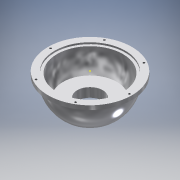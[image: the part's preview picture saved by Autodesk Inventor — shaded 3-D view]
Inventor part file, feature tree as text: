
AUTODESK INVENTOR PART (.ipt)
format: ipt  version: 2016 (Build 200138000, 138)  size: 551,424 bytes
history: native  units: mm
features: projected_geometry x22, sketch x21, extrude x16, plane x11, hole x5, mirror x3, loft x2, chamfer x2, pattern_circular x2, revolve x1, other x1
ambient origin geometry x8: Origin, YZ Plane, XZ Plane, XY Plane, X Axis, Y Axis, Z Axis, Center Point
bodies: Volumenkörper1 (feature_tree)
feature tree (86):
  revolve  "Umdrehung1"
  sketch  "Skizze6"  dims[d7=5.0mm d8=90.0deg]
  plane  "Arbeitsebene2"
  sketch  "Skizze7"  dims[d36=4.0mm d38=2.0mm]
  plane  "Arbeitsebene3"
  sketch  "Skizze8"  dims[d40=1.2mm d41=45.0mm]
  loft  "Erhebung1"
  extrude  "Extrusion16"  TaperAngle=90.0deg  [1 undecoded]
  other  "Rippe1"
  extrude  "Extrusion17"  Depth=2.0mm
  extrude  "Extrusion21"  Depth=45.0mm
  hole  "Bohrung4"  [1 undecoded]
  hole  "Bohrung3"  [1 undecoded]
  plane  "Arbeitsebene11"
  mirror  "Spiegeln6"
  mirror  "Spiegeln3"
  extrude  "Extrusion18"  TaperAngle=0.0deg  [1 undecoded]
  extrude  "Extrusion20"  Depth=51.0mm
  sketch  "Skizze37"  dims[d62=60.0deg]
  extrude  "Extrusion19"  Depth=53.0mm
  extrude  "Extrusion22"  Depth=10.0mm
  plane  "Arbeitsebene13"
  extrude  "Extrusion23"  Depth=8.0mm
  extrude  "Extrusion24"  Depth=3.0mm
  chamfer  "Fase3"  Distance=10.0mm
  chamfer  "Fase2"  Distance=7.0mm
  mirror  "Spiegeln8"
  plane  "Arbeitsebene14"
  plane  "Arbeitsebene1"
  hole  "Bohrung1"  [1 undecoded]
  plane  "Arbeitsebene17"
  extrude  "Extrusion29"  TaperAngle=90.0deg  [1 undecoded]
  extrude  "Extrusion28"  Depth=2.0mm
  extrude  "Extrusion31"  TaperAngle=90.0deg  [1 undecoded]
  plane  "Arbeitsebene18"
  loft  "Erhebung3"
  plane  "Arbeitsebene19"
  sketch  "Skizze57"  dims[d180=25.0mm]
  plane  "Arbeitsebene16"
  extrude  "Extrusion32"  Depth=2.0mm
  sketch  "Skizze61"  dims[d184=2.459mm d185=6.0mm d186=4.0mm d187=2.0mm d188=90.0deg d189=8.8mm d190=20.594885mm]
  extrude  "Extrusion34"  Depth=2.0mm TaperAngle=0.0deg
  hole  "Bohrung5"  [1 undecoded]
  pattern_circular  "Runde Anordnung1"  Angle=90.0deg  [1 undecoded]
  sketch  "Skizze62"  dims[d191=6.0mm]
  extrude  "Extrusion35"  Depth=2.0mm
  extrude  "Extrusion36"  Depth=10.0mm TaperAngle=0.0deg
  hole  "Bohrung6"  [1 undecoded]
  pattern_circular  "Runde Anordnung2"  [2 undecoded]
  plane  "Arbeitsebene20"
  sketch  "Skizze1"  dims[d3=5.0mm d5=50.0mm]
  projected_geometry  "Projizierte Kontur1"
  projected_geometry  "Projizierte Kontur3"
  projected_geometry  "Projizierte Kontur4"
  projected_geometry  "Projizierte Kontur5"
  projected_geometry  "Projizierte Kontur6"
  sketch  "Skizze13"  dims[d49=4.0mm d50=20.0mm]
  projected_geometry  "Projizierte Kontur10"
  sketch  "Skizze31"  dims[d51=5.0mm d53=10.0mm]
  sketch  "Skizze32"  dims[d54=0.0mm d55=90.0deg d56=0.0mm d57=90.0deg]
  projected_geometry  "Projizierte Kontur20"
  projected_geometry  "Projizierte Kontur22"
  projected_geometry  "Projizierte Kontur23"
  sketch  "Skizze39"  dims[d63=2.5mm d64=1.0mm d65=0.0mm d66=0.0mm d67=1.0mm d68=1.0mm d82=51.0mm]
  projected_geometry  "Projizierte Kontur24"
  projected_geometry  "Projizierte Kontur25"
  projected_geometry  "Projizierte Kontur28"
  projected_geometry  "Projizierte Kontur29"
  sketch  "Skizze44"  dims[d83=45.0mm d84=53.0mm]
  projected_geometry  "Projizierte Kontur31"
  sketch  "Skizze46"  dims[d85=60.0mm d87=360.0deg]
  projected_geometry  "Projizierte Kontur41"
  projected_geometry  "Projizierte Kontur42"
  projected_geometry  "Projizierte Kontur43"
  projected_geometry  "Projizierte Kontur49"
  sketch  "Skizze53"  dims[d89=2.459mm d90=8.0mm d91=4.0mm d92=2.0mm d93=90.0deg d94=10.0mm d95=20.594885mm d98=25.0mm]
  sketch  "Skizze54"  dims[d99=8.0mm d130=8.0mm]
  sketch  "Skizze55"  dims[d176=10.0mm d177=0.0mm d179=3.0mm]
  projected_geometry  "Projizierte Kontur50"
  projected_geometry  "Projizierte Kontur51"
  sketch  "Skizze60"  dims[d181=12.0mm d182=10.0mm d183=0.0mm]
  sketch  "Skizze63"  dims[d194=17.348736mm d201=7.0mm d202=0.0mm]
  projected_geometry  "Projizierte Kontur54"
  sketch  "Skizze64"  dims[d203=90.0deg d206=90.0deg]
  projected_geometry  "Projizierte Kontur55"
  sketch  "Skizze65"  dims[d207=5.25mm d208=90.0deg d209=3.490659mm d210=90.0deg d211=10.5mm d214=1.0mm d215=7.0mm d216=0.0mm d218=120.0deg d220=90.0deg d221=1.0mm d222=10.0mm d223=0.0mm d224=60.0deg d225=5.0mm d227=7.0mm d228=0.0mm d235=2.4mm d236=6.0mm d237=3.0mm d238=2.0mm d239=90.0deg d240=5.0mm d241=20.594885mm d242=7.0mm d243=0.0mm d244=5.0mm d245=2.0mm d246=4.0mm d247=3.0mm d248=15.0mm d249=0.0mm d252=3.0mm d253=1.0mm d255=5.0mm d257=15.0mm d258=0.0mm d262=11.0mm d263=5.0mm d264=45.0deg d266=1.0mm d268=1.5mm d269=9.699mm d270=5.0mm d271=45.0deg d272=0.0mm d277=0.8mm d292=10.0mm d293=6.0mm d294=37.5mm d295=13.919411mm d296=8.905149mm d297=27.925268mm d298=37.5mm d302=8.905149mm d303=0.0mm d304=17.0mm d305=10.0mm d306=0.0mm d310=22.0mm d311=5.0mm d312=0.0mm d313=17.0mm d314=0.0mm d315=90.0deg d316=0.0mm d317=90.0deg d318=10.5mm d325=0.0mm d326=8.0mm d327=4.363323mm d328=3.2mm d329=4.5mm d330=4.5mm d331=3.2mm d332=5.0mm d333=0.0mm d334=5.5mm d335=120.0deg d336=2.38157mm d339=2.5mm d340=0.0mm d341=3.2mm d342=6.0mm d343=4.0mm d344=2.0mm d345=90.0deg d346=8.0mm d347=20.594885mm d348=60.0mm d349=360.0deg d351=102.0mm d352=5.0mm d353=0.0mm d354=86.0mm d355=2.0mm d356=0.0mm d357=48.0mm d358=2.459mm d359=6.0mm d360=4.0mm d361=2.0mm d362=90.0deg d363=8.8mm d364=20.594885mm d365=60.0mm d366=360.0deg d368=20.0mm]
note: 12 required parameter values undecoded (feature->parameter linkage not recoverable at this tier; creation-order binding heuristic only, values carry confidence <= 0.55)
